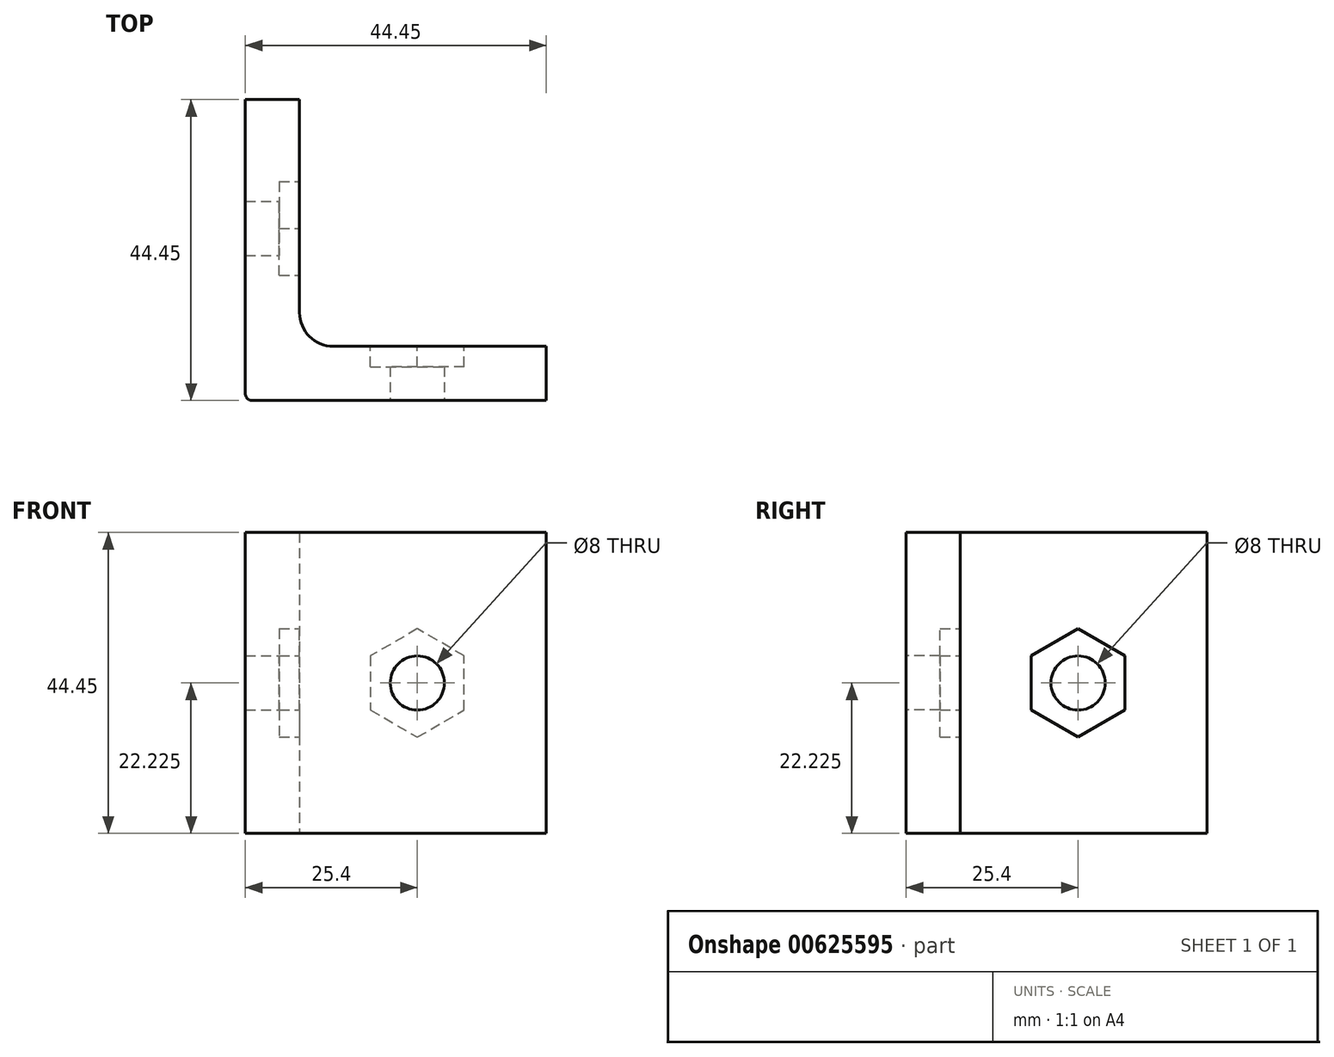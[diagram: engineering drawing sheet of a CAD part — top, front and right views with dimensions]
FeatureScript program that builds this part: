
annotation { "Feature Type Name" : "Feature", "Feature Type Description" : "" }
export const myFeature = defineFeature(function(context is Context, id is Id, definition is map)
    precondition{}
    {
        {
            var Q0;
            Q0=qCreatedBy(makeId("Top.planeOp"),FACE);
            var sketch = newSketch(context, id + "F0", { "sketchPlane" : qUnion([Q0])});
            skLineSegment(sketch, "E0", {"start": v(0, 44.45) * mm, "end": v(0, 1) * mm});
            skLineSegment(sketch, "E1", {"start": v(1, 0) * mm, "end": v(44.45, 0) * mm});
            skLineSegment(sketch, "E2", {"start": v(44.45, 0) * mm, "end": v(44.45, 8) * mm});
            skLineSegment(sketch, "E3", {"start": v(44.45, 8) * mm, "end": v(13, 8) * mm});
            skLineSegment(sketch, "E4", {"start": v(8, 13) * mm, "end": v(8, 44.45) * mm});
            skLineSegment(sketch, "E5", {"start": v(8, 44.45) * mm, "end": v(0, 44.45) * mm});
            skPoint(sketch, "E6.visualSharp", {"position": v(0, 0) * mm});
            skArc(sketch, "E6.filletArc", {"start": v(0, 1) * mm, "mid": v(0.3, 0.3) * mm, "end": v(1, 0) * mm});
            skPoint(sketch, "E7.visualSharp", {"position": v(8, 8) * mm});
            skArc(sketch, "E7.filletArc", {"start": v(8, 13) * mm, "mid": v(9.46, 9.46) * mm, "end": v(13, 8) * mm});
            skSolve(sketch);
        }
        {
            var Q0;
            Q0=qSketchRegion(id+"F0",true);
            extrude(context, id + "F1", {"entities" : qUnion([Q0]), "depth" : 44.45 * mm, "offsetDistance" : 25 * mm});
        }
        {
            var Q0;
            Q0=makeQuery(id+"F1.opExtrude","SWEPT_FACE",FACE,{"disambiguationData":[OSD([sQuery(id+"F0.wireOp",EDGE,"E4")])]});
            var sketch = newSketch(context, id + "F2", { "sketchPlane" : qUnion([Q0])});
            skLineSegment(sketch, "E8", {"start": v(44.45, 22.23) * mm, "end": v(0, 22.23) * mm, "construction": true});
            skCircle(sketch, "E9", {"center": v(25.4, 22.22) * mm, "radius": 4 * mm});
            skSolve(sketch);
        }
        {
            var Q0;
            Q0=qSketchRegion(id+"F2",true);
            extrude(context, id + "F3", {"entities" : qUnion([Q0]), "operationType" : NewBodyOperationType.REMOVE, "endBound" : BoundingType.UP_TO_NEXT, "oppositeDirection" : true, "depth" : 25 * mm, "offsetDistance" : 25 * mm});
        }
        {
            var Q0;
            Q0=makeQuery(id+"F1.opExtrude","SWEPT_FACE",FACE,{"disambiguationData":[OSD([sQuery(id+"F0.wireOp",EDGE,"E1")])]});
            var sketch = newSketch(context, id + "F4", { "sketchPlane" : qUnion([Q0])});
            skLineSegment(sketch, "E10", {"start": v(44.45, 22.23) * mm, "end": v(0, 22.23) * mm, "construction": true});
            skCircle(sketch, "E11", {"center": v(25.4, 22.22) * mm, "radius": 4 * mm});
            skSolve(sketch);
        }
        {
            var Q0;
            Q0=qSketchRegion(id+"F4",true);
            extrude(context, id + "F5", {"entities" : qUnion([Q0]), "operationType" : NewBodyOperationType.REMOVE, "endBound" : BoundingType.UP_TO_NEXT, "oppositeDirection" : true, "depth" : 25 * mm, "offsetDistance" : 25 * mm});
        }
        {
            var Q0;
            Q0=makeQuery(id+"F1.opExtrude","SWEPT_FACE",FACE,{"disambiguationData":[OSD([sQuery(id+"F0.wireOp",EDGE,"E4")])]});
            var sketch = newSketch(context, id + "F6", { "sketchPlane" : qUnion([Q0])});
            skCircle(sketch, "E12.cCircle", {"center": v(25.4, 22.22) * mm, "radius": 6.93 * mm, "construction": true});
            skLineSegment(sketch, "E12.0", {"start": v(32.33, 18.23) * mm, "end": v(25.4, 14.23) * mm});
            skLineSegment(sketch, "E12.1", {"start": v(25.4, 14.23) * mm, "end": v(18.47, 18.23) * mm});
            skLineSegment(sketch, "E12.2", {"start": v(18.47, 18.23) * mm, "end": v(18.47, 26.22) * mm});
            skLineSegment(sketch, "E12.3", {"start": v(18.47, 26.22) * mm, "end": v(25.4, 30.22) * mm});
            skLineSegment(sketch, "E12.4", {"start": v(25.4, 30.22) * mm, "end": v(32.33, 26.22) * mm});
            skLineSegment(sketch, "E12.5", {"start": v(32.33, 26.22) * mm, "end": v(32.33, 18.23) * mm});
            skPoint(sketch, "E12.0.midPoint", {"position": v(28.86, 16.23) * mm});
            skSolve(sketch);
        }
        {
            var Q0;
            Q0 = qSketchRegion(id + "F6", true);
            extrude(context, id + "F7", {"entities" : qUnion([Q0]), "operationType" : NewBodyOperationType.REMOVE, "oppositeDirection" : true, "depth" : 3 * mm, "offsetDistance" : 25 * mm});
        }
        {
            var Q0;
            Q0=makeQuery(id+"F1.opExtrude","SWEPT_FACE",FACE,{"disambiguationData":[OSD([sQuery(id+"F0.wireOp",EDGE,"E3")])]});
            var sketch = newSketch(context, id + "F8", { "sketchPlane" : qUnion([Q0])});
            skCircle(sketch, "E13.cCircle", {"center": v(-25.4, 22.22) * mm, "radius": 6.93 * mm, "construction": true});
            skLineSegment(sketch, "E13.0", {"start": v(-32.33, 26.22) * mm, "end": v(-25.4, 30.22) * mm});
            skLineSegment(sketch, "E13.1", {"start": v(-25.4, 30.22) * mm, "end": v(-18.47, 26.22) * mm});
            skLineSegment(sketch, "E13.2", {"start": v(-18.47, 26.22) * mm, "end": v(-18.47, 18.23) * mm});
            skLineSegment(sketch, "E13.3", {"start": v(-18.47, 18.23) * mm, "end": v(-25.4, 14.23) * mm});
            skLineSegment(sketch, "E13.4", {"start": v(-25.4, 14.23) * mm, "end": v(-32.33, 18.23) * mm});
            skLineSegment(sketch, "E13.5", {"start": v(-32.33, 18.23) * mm, "end": v(-32.33, 26.22) * mm});
            skPoint(sketch, "E13.0.midPoint", {"position": v(-28.86, 28.22) * mm});
            skSolve(sketch);
        }
        {
            var Q0;
            Q0 = qSketchRegion(id + "F8", true);
            extrude(context, id + "F9", {"entities" : qUnion([Q0]), "operationType" : NewBodyOperationType.REMOVE, "oppositeDirection" : true, "depth" : 3 * mm, "offsetDistance" : 25 * mm});
        }
    });
